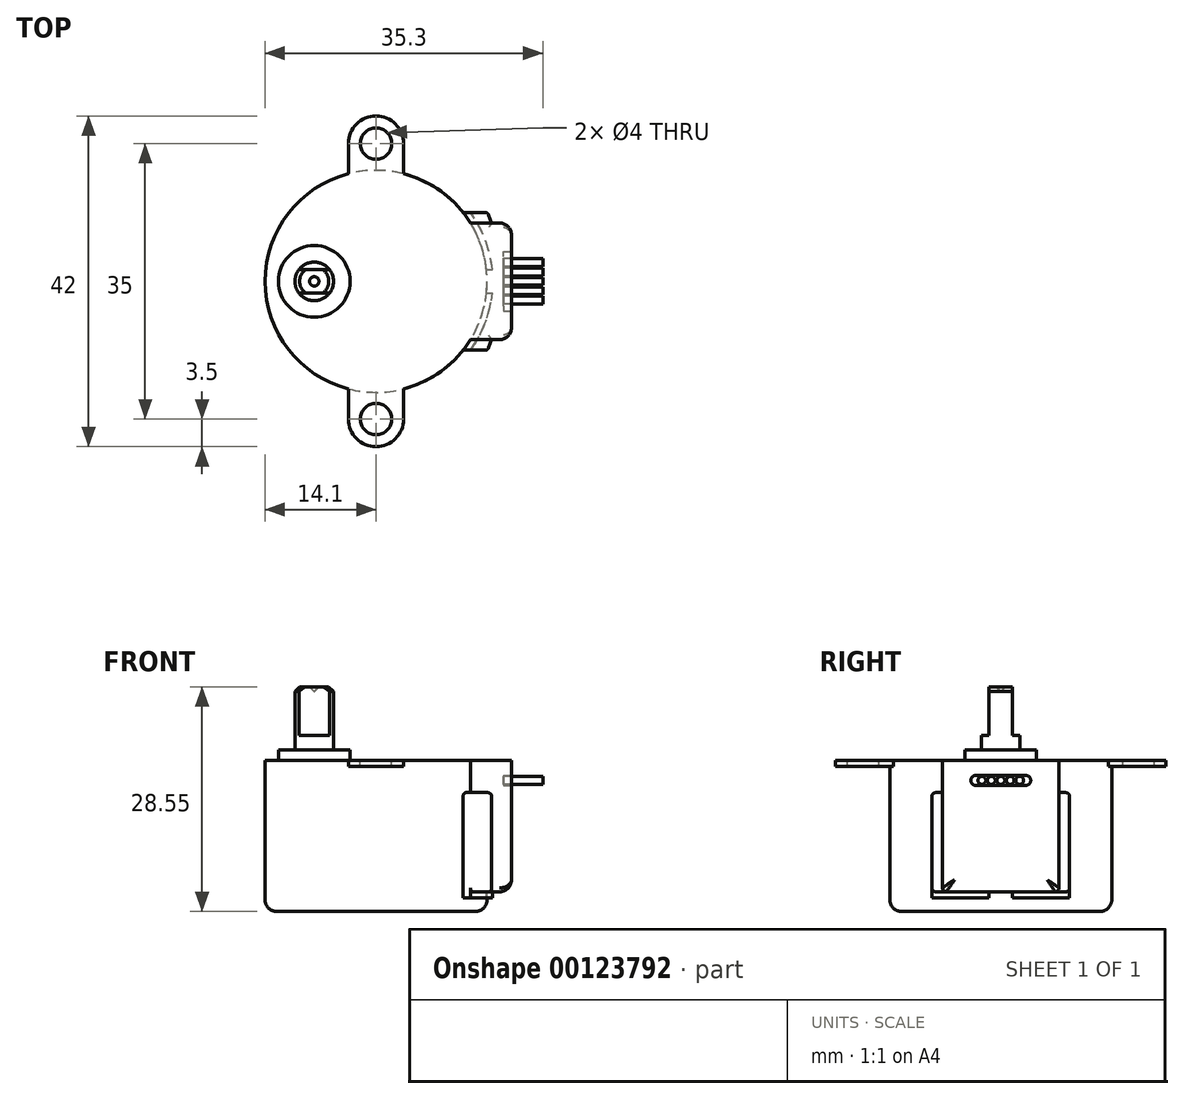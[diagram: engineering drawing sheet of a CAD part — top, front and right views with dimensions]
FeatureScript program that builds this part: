
annotation { "Feature Type Name" : "Feature", "Feature Type Description" : "" }
export const myFeature = defineFeature(function(context is Context, id is Id, definition is map)
    precondition{}
    {
        {
            var Q0;
            Q0=qCreatedBy(makeId("Front.planeOp"),FACE);
            var sketch = newSketch(context, id + "F0", { "sketchPlane" : qUnion([Q0])});
            skLineSegment(sketch, "E0", {"start": v(0, 0) * mm, "end": v(0, 8.75) * mm});
            skLineSegment(sketch, "E1", {"start": v(0.6, 9.35) * mm, "end": v(1.85, 9.35) * mm});
            skLineSegment(sketch, "E2", {"start": v(2.45, 8.75) * mm, "end": v(2.45, 1.35) * mm});
            skLineSegment(sketch, "E3", {"start": v(2.45, 1.35) * mm, "end": v(4.55, 1.35) * mm});
            skLineSegment(sketch, "E4", {"start": v(4.55, 1.35) * mm, "end": v(4.55, 0) * mm});
            skLineSegment(sketch, "E5", {"start": v(4.55, 0) * mm, "end": v(0, 0) * mm});
            skLineSegment(sketch, "E6", {"start": v(1.85, 9.35) * mm, "end": v(2.45, 8.75) * mm});
            skLineSegment(sketch, "E7", {"start": v(0.6, 9.35) * mm, "end": v(0, 8.75) * mm});
            skLineSegment(sketch, "E8", {"start": v(0, 8.75) * mm, "end": v(0, 13.35) * mm, "construction": true});
            skSolve(sketch);
        }
        {
            var Q0;
            Q0=makeQuery(id+"F0.imprint","IMPRINT",FACE,{"disambiguationData":[TD([[makeQuery(id+"F0.imprint","IMPRINT",EDGE,{"derivedFrom":sQuery(id+"F0.wireOp",EDGE,"E0")}),-1.0]])]});
            var Q1;
            Q1=sQuery(id+"F0.wireOp",EDGE,"E8");
            revolve(context, id + "F1", {"entities" : qUnion([Q0]), "axis" : qUnion([Q1]), "revolveType" : RevolveType.FULL});
        }
        {
            var Q0;
            Q0=makeQuery(id+"F1.opRevolve","SWEPT_FACE",FACE,{"disambiguationData":[OSD([sQuery(id+"F0.wireOp",EDGE,"E1")])]});
            var sketch = newSketch(context, id + "F2", { "sketchPlane" : qUnion([Q0])});
            skLineSegment(sketch, "E9", {"start": v(-3.37, 1.5) * mm, "end": v(3.8, 1.5) * mm});
            skLineSegment(sketch, "E10", {"start": v(3.8, 1.5) * mm, "end": v(3.8, 4.5) * mm});
            skLineSegment(sketch, "E11", {"start": v(3.8, 4.5) * mm, "end": v(-3.37, 4.5) * mm});
            skLineSegment(sketch, "E12", {"start": v(-3.37, 4.5) * mm, "end": v(-3.37, 1.5) * mm});
            skLineSegment(sketch, "E13", {"start": v(0, 0) * mm, "end": v(9.16, 0) * mm, "construction": true});
            skLineSegment(sketch, "E14.MirrorCS", {"start": v(-3.37, -4.5) * mm, "end": v(-3.37, -1.5) * mm});
            skLineSegment(sketch, "E15.MirrorCS", {"start": v(3.8, -4.5) * mm, "end": v(-3.37, -4.5) * mm});
            skLineSegment(sketch, "E16.MirrorCS", {"start": v(3.8, -1.5) * mm, "end": v(3.8, -4.5) * mm});
            skLineSegment(sketch, "E17.MirrorCS", {"start": v(-3.37, -1.5) * mm, "end": v(3.8, -1.5) * mm});
            skSolve(sketch);
        }
        {
            var Q0;
            Q0 = qSketchRegion(id + "F2", true);
            extrude(context, id + "F3", {"entities" : qUnion([Q0]), "operationType" : NewBodyOperationType.REMOVE, "oppositeDirection" : true, "depth" : 6.2 * mm});
        }
        {
            var Q0;
            Q0=makeQuery(id+"F1.opRevolve","SWEPT_FACE",FACE,{"disambiguationData":[OSD([sQuery(id+"F0.wireOp",EDGE,"E5")])]});
            var sketch = newSketch(context, id + "F4", { "sketchPlane" : qUnion([Q0])});
            skLineSegment(sketch, "E18", {"start": v(0, 0) * mm, "end": v(7.85, 0) * mm, "construction": true});
            skCircle(sketch, "E19", {"center": v(7.85, 0) * mm, "radius": 14.1 * mm});
            skLineSegment(sketch, "E20", {"start": v(0, 0) * mm, "end": v(-4.55, 0) * mm, "construction": true});
            skLineSegment(sketch, "E21", {"start": v(-4.55, 0) * mm, "end": v(-6.25, 0) * mm, "construction": true});
            skSolve(sketch);
        }
        {
            var Q0;
            Q0 = qSketchRegion(id + "F4", true);
            extrude(context, id + "F5", {"entities" : qUnion([Q0]), "depth" : 19.2 * mm});
        }
        {
            var Q0;
            Q0=makeQuery(id+"F5.opExtrude","CAP_FACE",FACE,{"disambiguationData":[OSD([sQuery(id+"F0.wireOp",EDGE,"E4"),sQuery(id+"F0.wireOp",EDGE,"E5"),sQuery(id+"F4.wireOp",EDGE,"E19")])],"isStart":true});
            var sketch = newSketch(context, id + "F6", { "sketchPlane" : qUnion([Q0])});
            skLineSegment(sketch, "E22", {"start": v(7.85, 0) * mm, "end": v(7.85, 17.5) * mm, "construction": true});
            skCircle(sketch, "E23", {"center": v(7.85, 17.5) * mm, "radius": 2 * mm});
            skArc(sketch, "E24", {"start": v(11.35, 17.5) * mm, "mid": v(7.85, 21) * mm, "end": v(4.35, 17.5) * mm});
            skLineSegment(sketch, "E25", {"start": v(7.85, 0) * mm, "end": v(11.35, 0) * mm, "construction": true});
            skLineSegment(sketch, "E26", {"start": v(11.35, 0) * mm, "end": v(11.35, 17.5) * mm});
            skLineSegment(sketch, "E27", {"start": v(7.85, 0) * mm, "end": v(4.35, 0) * mm, "construction": true});
            skLineSegment(sketch, "E28", {"start": v(4.35, 0) * mm, "end": v(4.35, 17.5) * mm});
            skLineSegment(sketch, "E29.MirrorCS", {"start": v(4.35, 0) * mm, "end": v(4.35, -17.5) * mm});
            skArc(sketch, "E30.MirrorCS", {"start": v(11.35, -17.5) * mm, "mid": v(7.85, -21) * mm, "end": v(4.35, -17.5) * mm});
            skCircle(sketch, "E31.MirrorC", {"center": v(7.85, -17.5) * mm, "radius": 2 * mm});
            skLineSegment(sketch, "E32.MirrorCS", {"start": v(11.35, 0) * mm, "end": v(11.35, -17.5) * mm});
            skSolve(sketch);
        }
        {
            var Q0;
            Q0 = qSketchRegion(id + "F6", true);
            extrude(context, id + "F7", {"entities" : qUnion([Q0]), "oppositeDirection" : true, "depth" : 0.75 * mm});
        }
        {
            var Q0;
            Q0=makeQuery(id+"F7.opExtrude","SWEPT_BODY",BODY,{"disambiguationData":[OSD([sQuery(id+"F6.wireOp",EDGE,"E23"),sQuery(id+"F6.wireOp",EDGE,"E24"),sQuery(id+"F6.wireOp",EDGE,"E26"),sQuery(id+"F6.wireOp",EDGE,"E28"),sQuery(id+"F6.wireOp",EDGE,"E29.MirrorCS"),sQuery(id+"F6.wireOp",EDGE,"E32.MirrorCS"),sQuery(id+"F6.wireOp",EDGE,"E30.MirrorCS"),sQuery(id+"F6.wireOp",EDGE,"E31.MirrorC")])]});
            var Q1;
            Q1=makeQuery(id+"F5.opExtrude","SWEPT_BODY",BODY,{"disambiguationData":[OSD([sQuery(id+"F0.wireOp",EDGE,"E4"),sQuery(id+"F0.wireOp",EDGE,"E5"),sQuery(id+"F4.wireOp",EDGE,"E19")])]});
            booleanBodies(context, id + "F8", {"operationType" : BooleanOperationType.UNION, "tools" : qUnion([Q0, Q1])});
        }
        {
            var Q0;
            Q0=makeQuery(id+"F8.opBoolean","MERGE",FACE,{"derivedFrom":[makeQuery(id+"F5.opExtrude","CAP_FACE",FACE,{"disambiguationData":[OSD([sQuery(id+"F4.wireOp",EDGE,"E19")])],"isStart":true}),makeQuery(id+"F7.opExtrude","CAP_FACE",FACE,{"disambiguationData":[OSD([sQuery(id+"F6.wireOp",EDGE,"E23"),sQuery(id+"F6.wireOp",EDGE,"E24"),sQuery(id+"F6.wireOp",EDGE,"E26"),sQuery(id+"F6.wireOp",EDGE,"E28"),sQuery(id+"F6.wireOp",EDGE,"E29.MirrorCS"),sQuery(id+"F6.wireOp",EDGE,"E32.MirrorCS"),sQuery(id+"F6.wireOp",EDGE,"E30.MirrorCS"),sQuery(id+"F6.wireOp",EDGE,"E31.MirrorC")])],"isStart":true})]});
            var sketch = newSketch(context, id + "F9", { "sketchPlane" : qUnion([Q0])});
            skLineSegment(sketch, "E33", {"start": v(7.85, 0) * mm, "end": v(25.05, 0) * mm, "construction": true});
            skPoint(sketch, "E33.endSnap0", {"position": v(21.95, 0) * mm});
            skLineSegment(sketch, "E34", {"start": v(25.05, 0) * mm, "end": v(25.05, 7.4) * mm});
            skLineSegment(sketch, "E35", {"start": v(25.05, 7.4) * mm, "end": v(7.85, 7.4) * mm});
            skLineSegment(sketch, "E36", {"start": v(7.85, 7.4) * mm, "end": v(7.85, 0) * mm});
            skLineSegment(sketch, "E37.MirrorCS", {"start": v(7.85, -7.4) * mm, "end": v(7.85, 0) * mm});
            skLineSegment(sketch, "E38.MirrorCS", {"start": v(25.05, -7.4) * mm, "end": v(7.85, -7.4) * mm});
            skLineSegment(sketch, "E39.MirrorCS", {"start": v(25.05, 0) * mm, "end": v(25.05, -7.4) * mm});
            skSolve(sketch);
        }
        {
            var Q0;
            {var subQ1=sQuery(id+"F9.wireOp",EDGE,"E34");Q0=makeQuery(id+"F9.imprint","IMPRINT",FACE,{"disambiguationData":[TD([[makeQuery(id+"F9.imprint","IMPRINT",EDGE,{"derivedFrom":subQ1}),1.0]])]});}
            extrude(context, id + "F10", {"entities" : qUnion([Q0]), "operationType" : NewBodyOperationType.ADD, "oppositeDirection" : true, "depth" : 16.7 * mm});
        }
        {
            var Q0;
            Q0=makeQuery(id+"F10.opExtrude","CAP_FACE",FACE,{"disambiguationData":[OSD([sQuery(id+"F4.wireOp",EDGE,"E19"),sQuery(id+"F9.wireOp",EDGE,"E34"),sQuery(id+"F9.wireOp",EDGE,"E35"),sQuery(id+"F9.wireOp",EDGE,"E38.MirrorCS"),sQuery(id+"F9.wireOp",EDGE,"E39.MirrorCS")])],"isStart":false});
            var sketch = newSketch(context, id + "F11", { "sketchPlane" : qUnion([Q0])});
            skLineSegment(sketch, "E40", {"start": v(25.05, 0) * mm, "end": v(21.95, 0) * mm, "construction": true});
            skLineSegment(sketch, "E41", {"start": v(22.55, 0) * mm, "end": v(22.55, 7.4) * mm});
            skLineSegment(sketch, "E42", {"start": v(22.55, 7.4) * mm, "end": v(22.05, 8.75) * mm});
            skLineSegment(sketch, "E43", {"start": v(22.05, 8.75) * mm, "end": v(18.9, 8.75) * mm});
            skLineSegment(sketch, "E44", {"start": v(18.9, 8.75) * mm, "end": v(18.9, 0) * mm});
            skLineSegment(sketch, "E45.MirrorCS", {"start": v(22.55, 0) * mm, "end": v(22.55, -7.4) * mm});
            skLineSegment(sketch, "E46.MirrorCS", {"start": v(22.55, -7.4) * mm, "end": v(22.05, -8.75) * mm});
            skLineSegment(sketch, "E47.MirrorCS", {"start": v(22.05, -8.75) * mm, "end": v(18.9, -8.75) * mm});
            skLineSegment(sketch, "E48.MirrorCS", {"start": v(18.9, -8.75) * mm, "end": v(18.9, 0) * mm});
            skSolve(sketch);
        }
        {
            var Q0;
            {var subQ3=sQuery(id+"F11.wireOp",EDGE,"E42");Q0=makeQuery(id+"F11.imprint","IMPRINT",FACE,{"disambiguationData":[TD([[makeQuery(id+"F11.imprint","IMPRINT",EDGE,{"derivedFrom":subQ3}),1.0]])]});}
            var Q1;
            {var subQ3=sQuery(id+"F11.wireOp",EDGE,"E41");Q1=makeQuery(id+"F11.imprint","IMPRINT",FACE,{"disambiguationData":[TD([[makeQuery(id+"F11.imprint","IMPRINT",EDGE,{"derivedFrom":subQ3}),1.0]])]});}
            extrude(context, id + "F12", {"entities" : qUnion([Q0, Q1]), "operationType" : NewBodyOperationType.ADD, "oppositeDirection" : true, "depth" : 12.6 * mm});
        }
        {
            var Q0;
            Q0=makeQuery(id+"F12.boolean.opBoolean","MERGE",FACE,{"derivedFrom":[makeQuery(id+"F10.opExtrude","CAP_FACE",FACE,{"disambiguationData":[OSD([sQuery(id+"F4.wireOp",EDGE,"E19"),sQuery(id+"F9.wireOp",EDGE,"E34"),sQuery(id+"F9.wireOp",EDGE,"E35"),sQuery(id+"F9.wireOp",EDGE,"E38.MirrorCS"),sQuery(id+"F9.wireOp",EDGE,"E39.MirrorCS")])],"isStart":false}),makeQuery(id+"F12.opExtrude","CAP_FACE",FACE,{"disambiguationData":[OSD([sQuery(id+"F11.wireOp",EDGE,"E41"),sQuery(id+"F11.wireOp",EDGE,"E42"),sQuery(id+"F11.wireOp",EDGE,"E43"),sQuery(id+"F11.wireOp",EDGE,"E44"),sQuery(id+"F11.wireOp",EDGE,"E45.MirrorCS"),sQuery(id+"F11.wireOp",EDGE,"E46.MirrorCS"),sQuery(id+"F11.wireOp",EDGE,"E47.MirrorCS"),sQuery(id+"F11.wireOp",EDGE,"E48.MirrorCS")])],"isStart":true})]});
            var sketch = newSketch(context, id + "F13", { "sketchPlane" : qUnion([Q0])});
            skLineSegment(sketch, "E49", {"start": v(25.05, 0) * mm, "end": v(7.85, 0) * mm, "construction": true});
            skArc(sketch, "E50", {"start": v(18.9, -8.75) * mm, "mid": v(20.9, -5.33) * mm, "end": v(21.87, -1.5) * mm});
            skArc(sketch, "E51", {"start": v(19.84, -8.75) * mm, "mid": v(21.71, -5.3) * mm, "end": v(22.62, -1.5) * mm});
            skLineSegment(sketch, "E52", {"start": v(18.9, -8.75) * mm, "end": v(19.84, -8.75) * mm});
            skLineSegment(sketch, "E53", {"start": v(21.87, -1.5) * mm, "end": v(22.62, -1.5) * mm});
            skLineSegment(sketch, "E54.MirrorCS", {"start": v(21.87, 1.5) * mm, "end": v(22.62, 1.5) * mm});
            skArc(sketch, "E55.MirrorCS", {"start": v(19.84, 8.75) * mm, "mid": v(21.71, 5.3) * mm, "end": v(22.62, 1.5) * mm});
            skArc(sketch, "E56.MirrorCS", {"start": v(18.9, 8.75) * mm, "mid": v(20.9, 5.33) * mm, "end": v(21.87, 1.5) * mm});
            skLineSegment(sketch, "E57.MirrorCS", {"start": v(18.9, 8.75) * mm, "end": v(19.84, 8.75) * mm});
            skSolve(sketch);
        }
        {
            var Q0;
            Q0=makeQuery(id+"F13.imprint","IMPRINT",FACE,{"disambiguationData":[TD([[makeQuery(id+"F13.imprint","IMPRINT",EDGE,{"derivedFrom":sQuery(id+"F13.wireOp",EDGE,"E50")}),-1.0]])]});
            var Q1;
            Q1=makeQuery(id+"F13.imprint","IMPRINT",FACE,{"disambiguationData":[TD([[makeQuery(id+"F13.imprint","IMPRINT",EDGE,{"derivedFrom":sQuery(id+"F13.wireOp",EDGE,"E54.MirrorCS")}),1.0]])]});
            extrude(context, id + "F14", {"entities" : qUnion([Q0, Q1]), "operationType" : NewBodyOperationType.ADD, "depth" : 0.75 * mm});
        }
        {
            var Q0;
            Q0=makeQuery(id+"F10.opExtrude","SWEPT_EDGE",EDGE,{"disambiguationData":[OSD([sQuery(id+"F9.wireOp",EDGE,"E38.MirrorCS"),sQuery(id+"F9.wireOp",EDGE,"E39.MirrorCS")])]});
            var Q1;
            Q1=makeQuery(id+"F10.opExtrude","SWEPT_EDGE",EDGE,{"disambiguationData":[OSD([sQuery(id+"F9.wireOp",EDGE,"E34"),sQuery(id+"F9.wireOp",EDGE,"E35")])]});
            var Q2;
            Q2=makeQuery(id+"F10.opExtrude","CAP_EDGE",EDGE,{"disambiguationData":[OSD([sQuery(id+"F9.wireOp",EDGE,"E34"),sQuery(id+"F9.wireOp",EDGE,"E39.MirrorCS")])],"isStart":false});
            var Q3;
            Q3=makeQuery(id+"F5.opExtrude","CAP_EDGE",EDGE,{"disambiguationData":[OSD([sQuery(id+"F4.wireOp",EDGE,"E19")])],"isStart":false});
            fillet(context, id + "F15", {"entities" : qUnion([Q0, Q1, Q2, Q3]), "radius" : 1.5 * mm, "tangentPropagation" : true, "allowEdgeOverflow" : false});
        }
        {
            var Q0;
            Q0=makeQuery(id+"F10.opExtrude","CAP_EDGE",EDGE,{"disambiguationData":[OSD([sQuery(id+"F9.wireOp",EDGE,"E35")])],"isStart":false});
            var Q1;
            Q1=makeQuery(id+"F12.opExtrude","CAP_EDGE",EDGE,{"disambiguationData":[OSD([sQuery(id+"F11.wireOp",EDGE,"E46.MirrorCS")])],"isStart":true});
            var Q2;
            Q2=makeQuery(id+"F12.opExtrude","CAP_EDGE",EDGE,{"disambiguationData":[OSD([sQuery(id+"F11.wireOp",EDGE,"E47.MirrorCS")])],"isStart":true});
            var Q3;
            Q3=makeQuery(id+"F12.opExtrude","SWEPT_EDGE",EDGE,{"disambiguationData":[OSD([sQuery(id+"F11.wireOp",EDGE,"E46.MirrorCS"),sQuery(id+"F11.wireOp",EDGE,"E47.MirrorCS")])]});
            var Q4;
            Q4=makeQuery(id+"F12.opExtrude","CAP_EDGE",EDGE,{"disambiguationData":[OSD([sQuery(id+"F11.wireOp",EDGE,"E46.MirrorCS")])],"isStart":false});
            var Q5;
            Q5=makeQuery(id+"F12.opExtrude","CAP_EDGE",EDGE,{"disambiguationData":[OSD([sQuery(id+"F11.wireOp",EDGE,"E47.MirrorCS")])],"isStart":false});
            var Q6;
            Q6=makeQuery(id+"F10.opExtrude","CAP_EDGE",EDGE,{"disambiguationData":[OSD([sQuery(id+"F9.wireOp",EDGE,"E38.MirrorCS")])],"isStart":false});
            var Q7;
            Q7=makeQuery(id+"F12.opExtrude","CAP_EDGE",EDGE,{"disambiguationData":[OSD([sQuery(id+"F11.wireOp",EDGE,"E42")])],"isStart":true});
            var Q8;
            Q8=makeQuery(id+"F12.opExtrude","CAP_EDGE",EDGE,{"disambiguationData":[OSD([sQuery(id+"F11.wireOp",EDGE,"E43")])],"isStart":true});
            var Q9;
            Q9=makeQuery(id+"F12.opExtrude","SWEPT_EDGE",EDGE,{"disambiguationData":[OSD([sQuery(id+"F11.wireOp",EDGE,"E42"),sQuery(id+"F11.wireOp",EDGE,"E43")])]});
            var Q10;
            Q10=makeQuery(id+"F12.opExtrude","CAP_EDGE",EDGE,{"disambiguationData":[OSD([sQuery(id+"F11.wireOp",EDGE,"E42")])],"isStart":false});
            var Q11;
            Q11=makeQuery(id+"F12.opExtrude","CAP_EDGE",EDGE,{"disambiguationData":[OSD([sQuery(id+"F11.wireOp",EDGE,"E43")])],"isStart":false});
            fillet(context, id + "F16", {"entities" : qUnion([Q0, Q1, Q2, Q3, Q4, Q5, Q6, Q7, Q8, Q9, Q10, Q11]), "radius" : 0.5 * mm, "tangentPropagation" : true, "allowEdgeOverflow" : false});
        }
        {
            var Q0;
            Q0=makeQuery(id+"F10.opExtrude","SWEPT_FACE",FACE,{"disambiguationData":[OSD([sQuery(id+"F9.wireOp",EDGE,"E34"),sQuery(id+"F9.wireOp",EDGE,"E39.MirrorCS")])]});
            var sketch = newSketch(context, id + "F17", { "sketchPlane" : qUnion([Q0])});
            skLineSegment(sketch, "E58", {"start": v(0, 0) * mm, "end": v(0, -2.55) * mm, "construction": true});
            skLineSegment(sketch, "E59", {"start": v(0, -2.55) * mm, "end": v(-3.15, -2.55) * mm, "construction": true});
            skArc(sketch, "E60", {"start": v(-3.15, -1.9) * mm, "mid": v(-3.8, -2.55) * mm, "end": v(-3.15, -3.2) * mm});
            skLineSegment(sketch, "E61", {"start": v(-3.15, -1.9) * mm, "end": v(0, -1.9) * mm});
            skPoint(sketch, "E61.endSnap0", {"position": v(0, -1.27) * mm});
            skLineSegment(sketch, "E62", {"start": v(-3.15, -3.2) * mm, "end": v(0, -3.2) * mm});
            skLineSegment(sketch, "E63.MirrorCS", {"start": v(3.15, -1.9) * mm, "end": v(0, -1.9) * mm});
            skArc(sketch, "E64.MirrorCS", {"start": v(3.15, -1.9) * mm, "mid": v(3.8, -2.55) * mm, "end": v(3.15, -3.2) * mm});
            skLineSegment(sketch, "E65.MirrorCS", {"start": v(3.15, -3.2) * mm, "end": v(0, -3.2) * mm});
            skSolve(sketch);
        }
        {
            var Q0;
            Q0=makeQuery(id+"F17.imprint","IMPRINT",FACE,{"disambiguationData":[TD([[makeQuery(id+"F17.imprint","IMPRINT",EDGE,{"derivedFrom":sQuery(id+"F17.wireOp",EDGE,"E60")}),1.0]])]});
            extrude(context, id + "F18", {"entities" : qUnion([Q0]), "operationType" : NewBodyOperationType.REMOVE, "oppositeDirection" : true, "depth" : 1 * mm});
        }
        {
            var Q0;
            Q0=makeQuery(id+"F18.boolean.opBoolean","COPY",FACE,{"derivedFrom":makeQuery(id+"F18.opExtrude","CAP_FACE",FACE,{"disambiguationData":[OSD([sQuery(id+"F17.wireOp",EDGE,"E60"),sQuery(id+"F17.wireOp",EDGE,"E61"),sQuery(id+"F17.wireOp",EDGE,"E62"),sQuery(id+"F17.wireOp",EDGE,"E63.MirrorCS"),sQuery(id+"F17.wireOp",EDGE,"E64.MirrorCS"),sQuery(id+"F17.wireOp",EDGE,"E65.MirrorCS")])],"isStart":false})});
            var sketch = newSketch(context, id + "F19", { "sketchPlane" : qUnion([Q0])});
            skLineSegment(sketch, "E66", {"start": v(0, -3.2) * mm, "end": v(0, -1.9) * mm, "construction": true});
            skLineSegment(sketch, "E67", {"start": v(0, -2.55) * mm, "end": v(1.2, -2.55) * mm, "construction": true});
            skLineSegment(sketch, "E68", {"start": v(1.2, -2.55) * mm, "end": v(2.4, -2.55) * mm, "construction": true});
            skLineSegment(sketch, "E69", {"start": v(0, -2.55) * mm, "end": v(-1.2, -2.55) * mm, "construction": true});
            skLineSegment(sketch, "E70", {"start": v(-1.2, -2.55) * mm, "end": v(-2.4, -2.55) * mm, "construction": true});
            skCircle(sketch, "E71", {"center": v(0, -2.55) * mm, "radius": 0.5 * mm});
            skCircle(sketch, "E72", {"center": v(-1.2, -2.55) * mm, "radius": 0.5 * mm});
            skCircle(sketch, "E73", {"center": v(-2.4, -2.55) * mm, "radius": 0.5 * mm});
            skCircle(sketch, "E74", {"center": v(1.2, -2.55) * mm, "radius": 0.5 * mm});
            skCircle(sketch, "E75", {"center": v(2.4, -2.55) * mm, "radius": 0.5 * mm});
            skSolve(sketch);
        }
        {
            var Q0;
            Q0=makeQuery(id+"F19.imprint","IMPRINT",FACE,{"disambiguationData":[TD([[makeQuery(id+"F19.imprint","IMPRINT",EDGE,{"derivedFrom":sQuery(id+"F19.wireOp",EDGE,"E73")}),1.0]])]});
            extrude(context, id + "F20", {"entities" : qUnion([Q0]), "depth" : 5 * mm});
        }
        {
            var Q0;
            Q0=makeQuery(id+"F19.imprint","IMPRINT",FACE,{"disambiguationData":[TD([[makeQuery(id+"F19.imprint","IMPRINT",EDGE,{"derivedFrom":sQuery(id+"F19.wireOp",EDGE,"E72")}),1.0]])]});
            extrude(context, id + "F21", {"entities" : qUnion([Q0]), "depth" : 5 * mm});
        }
        {
            var Q0;
            Q0=makeQuery(id+"F19.imprint","IMPRINT",FACE,{"disambiguationData":[TD([[makeQuery(id+"F19.imprint","IMPRINT",EDGE,{"derivedFrom":sQuery(id+"F19.wireOp",EDGE,"E71")}),1.0]])]});
            extrude(context, id + "F22", {"entities" : qUnion([Q0]), "depth" : 5 * mm});
        }
        {
            var Q0;
            Q0=makeQuery(id+"F19.imprint","IMPRINT",FACE,{"disambiguationData":[TD([[makeQuery(id+"F19.imprint","IMPRINT",EDGE,{"derivedFrom":sQuery(id+"F19.wireOp",EDGE,"E74")}),1.0]])]});
            extrude(context, id + "F23", {"entities" : qUnion([Q0]), "depth" : 5 * mm});
        }
        {
            var Q0;
            Q0=makeQuery(id+"F19.imprint","IMPRINT",FACE,{"disambiguationData":[TD([[makeQuery(id+"F19.imprint","IMPRINT",EDGE,{"derivedFrom":sQuery(id+"F19.wireOp",EDGE,"E75")}),1.0]])]});
            extrude(context, id + "F24", {"entities" : qUnion([Q0]), "depth" : 5 * mm});
        }
    });
